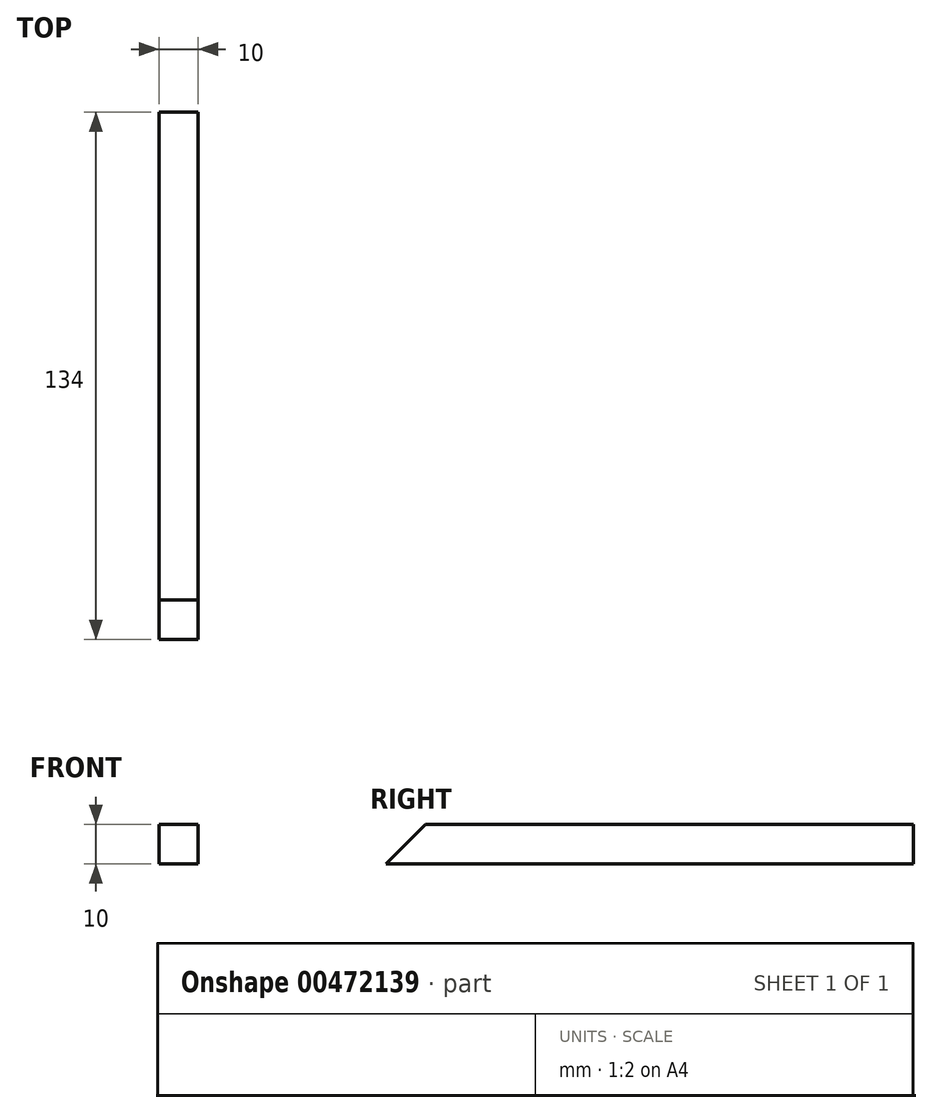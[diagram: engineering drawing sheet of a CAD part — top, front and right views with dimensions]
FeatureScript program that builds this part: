
annotation { "Feature Type Name" : "Feature", "Feature Type Description" : "" }
export const myFeature = defineFeature(function(context is Context, id is Id, definition is map)
    precondition{}
    {
        {
            var Q0;
            Q0=qCreatedBy(makeId("Front.planeOp"),FACE);
            var sketch = newSketch(context, id + "F0", { "sketchPlane" : qUnion([Q0])});
            skLineSegment(sketch, "E0.bottom", {"start": v(5, -5) * mm, "end": v(-5, -5) * mm});
            skLineSegment(sketch, "E0.top", {"start": v(5, 5) * mm, "end": v(-5, 5) * mm});
            skLineSegment(sketch, "E0.left", {"start": v(5, -5) * mm, "end": v(5, 5) * mm});
            skLineSegment(sketch, "E0.right", {"start": v(-5, -5) * mm, "end": v(-5, 5) * mm});
            skPoint(sketch, "E0.middle", {"position": v(0, 0) * mm});
            skSolve(sketch);
        }
        {
            var Q0;
            Q0=makeQuery(id+"F0.imprint","IMPRINT",FACE,{"disambiguationData":[TD([[makeQuery(id+"F0.imprint","IMPRINT",EDGE,{"derivedFrom":sQuery(id+"F0.wireOp",EDGE,"E0.bottom")}),-1.0]])]});
            extrude(context, id + "F1", {"entities" : qUnion([Q0]), "depth" : 134 * mm});
        }
        {
            var Q0;
            Q0=makeQuery(id+"F1.opExtrude","CAP_EDGE",EDGE,{"disambiguationData":[OSD([sQuery(id+"F0.wireOp",EDGE,"E0.top")])],"isStart":false});
            chamfer(context, id + "F2", {"entities" : qUnion([Q0]), "width" : 10 * mm, "tangentPropagation" : true});
        }
        {
            var Q0;
            Q0=makeQuery(id+"F1.opExtrude","SWEPT_FACE",FACE,{"disambiguationData":[OSD([sQuery(id+"F0.wireOp",EDGE,"E0.left")])]});
            var sketch = newSketch(context, id + "F3", { "sketchPlane" : qUnion([Q0])});
            skPoint(sketch, "E1", {"position": v(-10, 5) * mm});
            skLineSegment(sketch, "E2", {"start": v(-10, 5) * mm, "end": v(-10, -5) * mm, "construction": true});
            skSolve(sketch);
        }
    });
